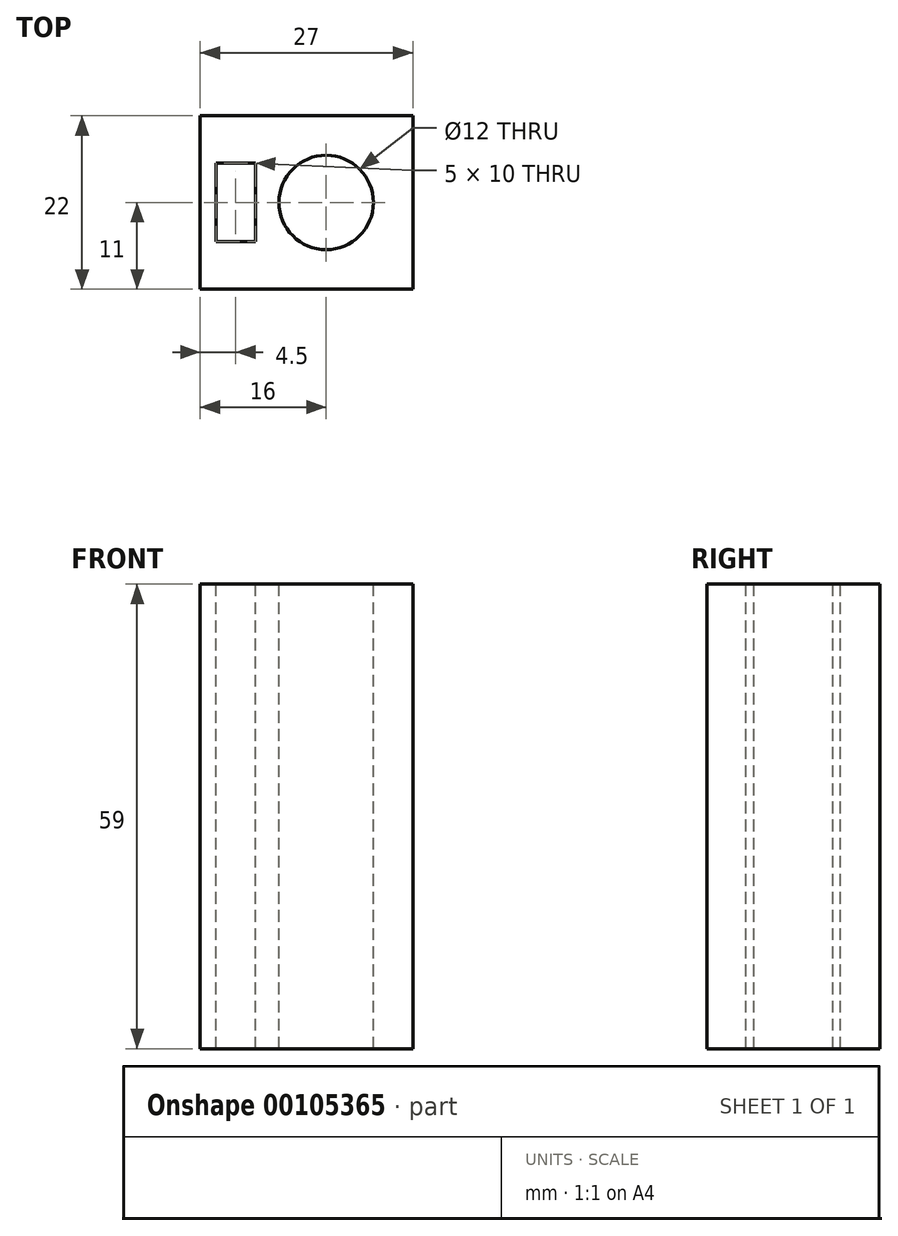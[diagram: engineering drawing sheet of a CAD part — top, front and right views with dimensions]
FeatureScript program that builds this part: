
annotation { "Feature Type Name" : "Feature", "Feature Type Description" : "" }
export const myFeature = defineFeature(function(context is Context, id is Id, definition is map)
    precondition{}
    {
        {
            var Q0;
            Q0=qCreatedBy(makeId("Top.planeOp"),FACE);
            var sketch = newSketch(context, id + "F0", { "sketchPlane" : qUnion([Q0])});
            skLineSegment(sketch, "E0.bottom", {"start": v(-13.5, 11) * mm, "end": v(13.5, 11) * mm});
            skLineSegment(sketch, "E0.top", {"start": v(-13.5, -11) * mm, "end": v(13.5, -11) * mm});
            skLineSegment(sketch, "E0.left", {"start": v(-13.5, 11) * mm, "end": v(-13.5, -11) * mm});
            skLineSegment(sketch, "E0.right", {"start": v(13.5, 11) * mm, "end": v(13.5, -11) * mm});
            skSolve(sketch);
        }
        {
            var Q0;
            Q0=makeQuery(id+"F0.imprint","IMPRINT",FACE,{"disambiguationData":[TD([[makeQuery(id+"F0.imprint","IMPRINT",EDGE,{"derivedFrom":sQuery(id+"F0.wireOp",EDGE,"E0.bottom")}),-1.0]])]});
            extrude(context, id + "F1", {"entities" : qUnion([Q0]), "depth" : (59 / 2) * mm, "hasSecondDirection" : true, "secondDirectionOppositeDirection" : true, "secondDirectionDepth" : 29.5 * mm});
        }
        {
            var Q0;
            Q0=makeQuery(id+"F1.opExtrude","CAP_FACE",FACE,{"disambiguationData":[OSD([sQuery(id+"F0.wireOp",EDGE,"E0.bottom"),sQuery(id+"F0.wireOp",EDGE,"E0.top"),sQuery(id+"F0.wireOp",EDGE,"E0.left"),sQuery(id+"F0.wireOp",EDGE,"E0.right")])],"isStart":false});
            var sketch = newSketch(context, id + "F2", { "sketchPlane" : qUnion([Q0])});
            skCircle(sketch, "E1", {"center": v(2.5, 0) * mm, "radius": 6 * mm});
            skSolve(sketch);
        }
        {
            var Q0;
            Q0=qSketchRegion(id+"F2",true);
            extrude(context, id + "F3", {"entities" : qUnion([Q0]), "operationType" : NewBodyOperationType.REMOVE, "endBound" : BoundingType.UP_TO_NEXT, "oppositeDirection" : true, "depth" : 25 * mm});
        }
        {
            var Q0;
            Q0=makeQuery(id+"F1.opExtrude","CAP_FACE",FACE,{"disambiguationData":[OSD([sQuery(id+"F0.wireOp",EDGE,"E0.bottom"),sQuery(id+"F0.wireOp",EDGE,"E0.top"),sQuery(id+"F0.wireOp",EDGE,"E0.left"),sQuery(id+"F0.wireOp",EDGE,"E0.right")])],"isStart":false});
            var sketch = newSketch(context, id + "F4", { "sketchPlane" : qUnion([Q0])});
            skLineSegment(sketch, "E2.bottom", {"start": v(-6.5, 5) * mm, "end": v(-11.5, 5) * mm});
            skLineSegment(sketch, "E2.top", {"start": v(-6.5, -5) * mm, "end": v(-11.5, -5) * mm});
            skLineSegment(sketch, "E2.left", {"start": v(-6.5, 5) * mm, "end": v(-6.5, -5) * mm});
            skLineSegment(sketch, "E2.right", {"start": v(-11.5, 5) * mm, "end": v(-11.5, -5) * mm});
            skSolve(sketch);
        }
        {
            var Q0;
            Q0=qSketchRegion(id+"F4",true);
            extrude(context, id + "F5", {"entities" : qUnion([Q0]), "operationType" : NewBodyOperationType.REMOVE, "endBound" : BoundingType.UP_TO_NEXT, "oppositeDirection" : true, "depth" : 25 * mm});
        }
    });
